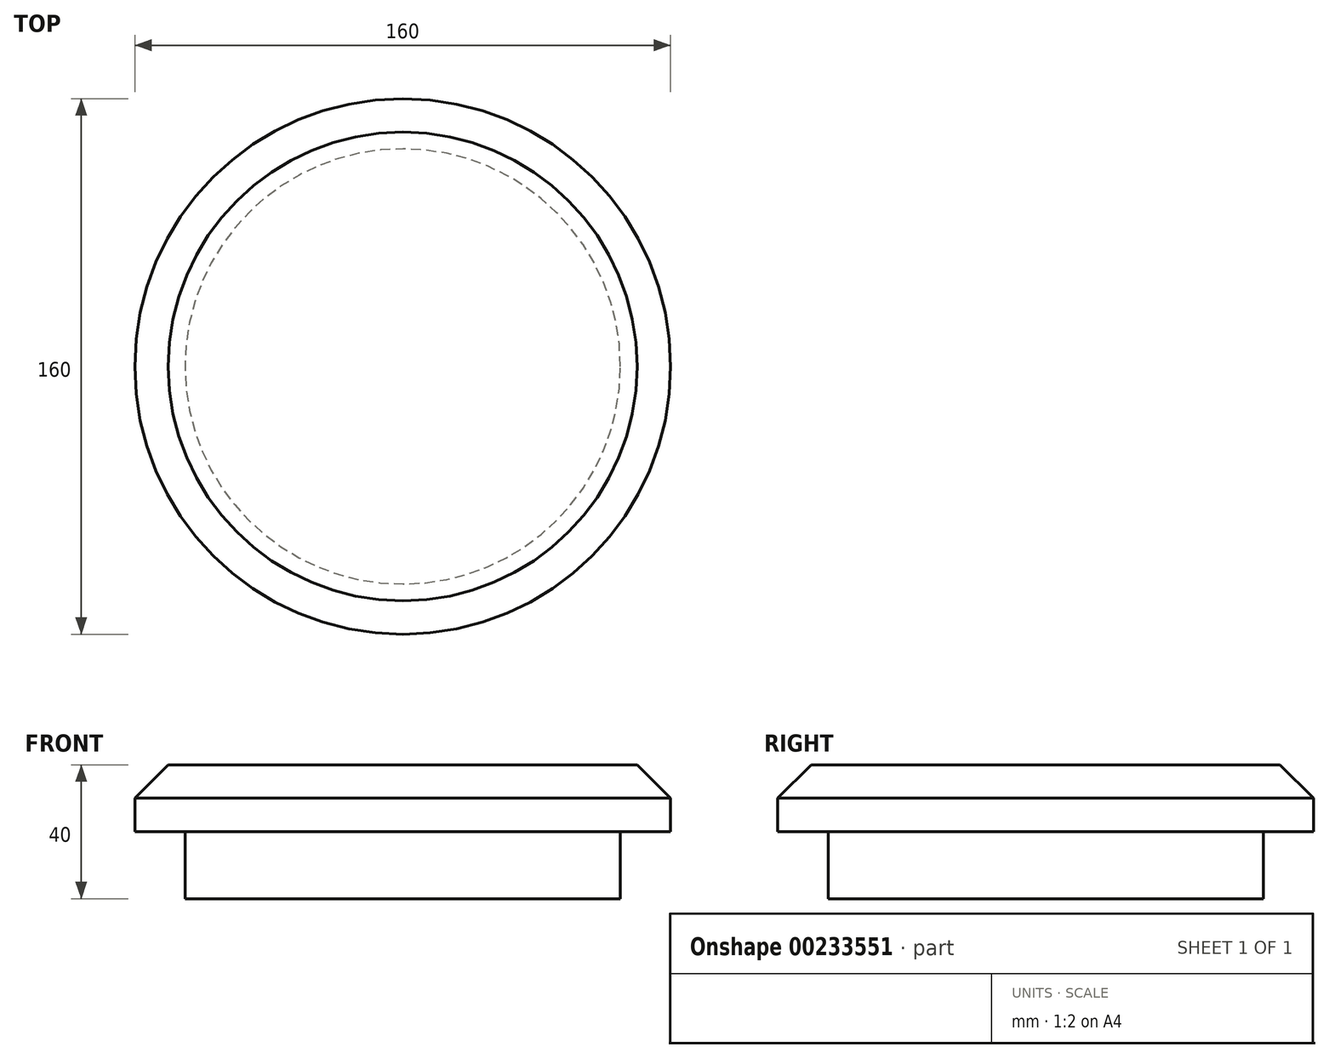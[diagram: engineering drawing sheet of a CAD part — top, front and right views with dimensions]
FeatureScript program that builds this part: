
annotation { "Feature Type Name" : "Feature", "Feature Type Description" : "" }
export const myFeature = defineFeature(function(context is Context, id is Id, definition is map)
    precondition{}
    {
        {
            var Q0;
            Q0=qCreatedBy(makeId("Front.planeOp"),FACE);
            var sketch = newSketch(context, id + "F0", { "sketchPlane" : qUnion([Q0])});
            skLineSegment(sketch, "E0", {"start": v(0, 0) * mm, "end": v(-65, 0) * mm});
            skLineSegment(sketch, "E1", {"start": v(-65, 0) * mm, "end": v(-65, 20) * mm});
            skLineSegment(sketch, "E2", {"start": v(-65, 20) * mm, "end": v(-80, 20) * mm});
            skLineSegment(sketch, "E3", {"start": v(-80, 20) * mm, "end": v(-80, 40) * mm});
            skLineSegment(sketch, "E4", {"start": v(-80, 40) * mm, "end": v(0, 40) * mm});
            skLineSegment(sketch, "E5", {"start": v(0, 40) * mm, "end": v(0, 0) * mm});
            skSolve(sketch);
        }
        {
            var Q0;
            Q0=makeQuery(id+"F0.imprint","IMPRINT",FACE,{"disambiguationData":[TD([[makeQuery(id+"F0.imprint","IMPRINT",EDGE,{"derivedFrom":sQuery(id+"F0.wireOp",EDGE,"E0")}),-1.0]])]});
            var Q1;
            Q1=sQuery(id+"F0.wireOp",EDGE,"E5");
            revolve(context, id + "F1", {"entities" : qUnion([Q0]), "axis" : qUnion([Q1]), "revolveType" : RevolveType.FULL});
        }
        {
            var Q0;
            Q0=makeQuery(id+"F1.opRevolve","SWEPT_EDGE",EDGE,{"disambiguationData":[OSD([sQuery(id+"F0.wireOp",EDGE,"E3"),sQuery(id+"F0.wireOp",EDGE,"E4")])]});
            chamfer(context, id + "F2", {"entities" : qUnion([Q0]), "chamferType" : ChamferType.OFFSET_ANGLE, "width" : 10 * mm, "oppositeDirection" : false, "angle" : 45 * degree, "tangentPropagation" : true});
        }
    });
